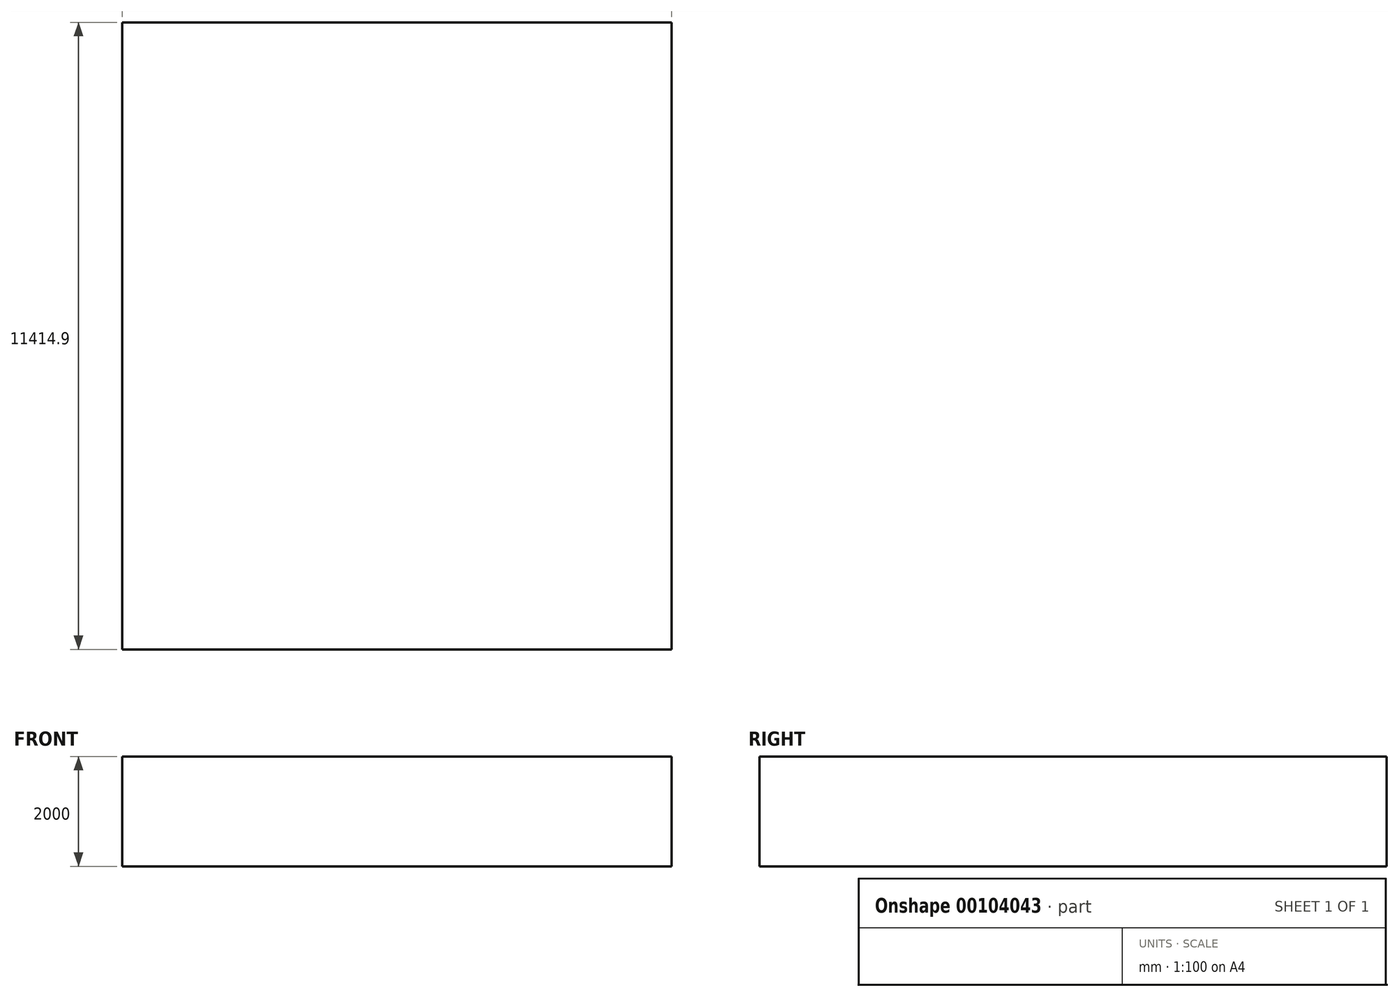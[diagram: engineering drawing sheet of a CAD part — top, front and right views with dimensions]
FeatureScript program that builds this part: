
annotation { "Feature Type Name" : "Feature", "Feature Type Description" : "" }
export const myFeature = defineFeature(function(context is Context, id is Id, definition is map)
    precondition{}
    {
        {
            var Q0;
            Q0=qCreatedBy(makeId("Top.planeOp"),FACE);
            var sketch = newSketch(context, id + "F0", { "sketchPlane" : qUnion([Q0])});
            skLineSegment(sketch, "E0.bottom", {"start": v(5000, 5707.45) * mm, "end": v(-5000, 5707.45) * mm});
            skLineSegment(sketch, "E0.top", {"start": v(5000, -5707.45) * mm, "end": v(-5000, -5707.45) * mm});
            skLineSegment(sketch, "E0.left", {"start": v(5000, 5707.45) * mm, "end": v(5000, -5707.45) * mm});
            skLineSegment(sketch, "E0.right", {"start": v(-5000, 5707.45) * mm, "end": v(-5000, -5707.45) * mm});
            skPoint(sketch, "E0.middle", {"position": v(0, 0) * mm});
            skSolve(sketch);
        }
        {
            var Q0;
            Q0 = qSketchRegion(id + "F0", true);
            extrude(context, id + "F1", {"entities" : qUnion([Q0]), "depth" : 2000 * mm});
        }
    });
